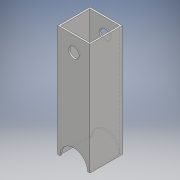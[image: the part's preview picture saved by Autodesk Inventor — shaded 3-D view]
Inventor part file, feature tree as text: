
AUTODESK INVENTOR PART (.ipt)
format: ipt  version: 2018 (Build 220112000, 112)  size: 120,832 bytes
history: native  units: mm
features: sketch x4, extrude x2, other x1, hole x1
ambient origin geometry x8: Origin, YZ Plane, XZ Plane, XY Plane, X Axis, Y Axis, Z Axis, Center Point
bodies: Body1 (feature_tree)
feature tree (8):
  other  "ソリッド1"
  extrude  "押し出し1"  Depth=32.0mm
  extrude  "押し出し2"  Depth=32.0mm
  hole  "穴1"  [1 undecoded]
  sketch  "スケッチ4"
  sketch  "スケッチ1"
  sketch  "スケッチ2"
  sketch  "スケッチ3"
note: 1 required parameter value undecoded (feature->parameter linkage not recoverable at this tier; creation-order binding heuristic only, values carry confidence <= 0.55)
